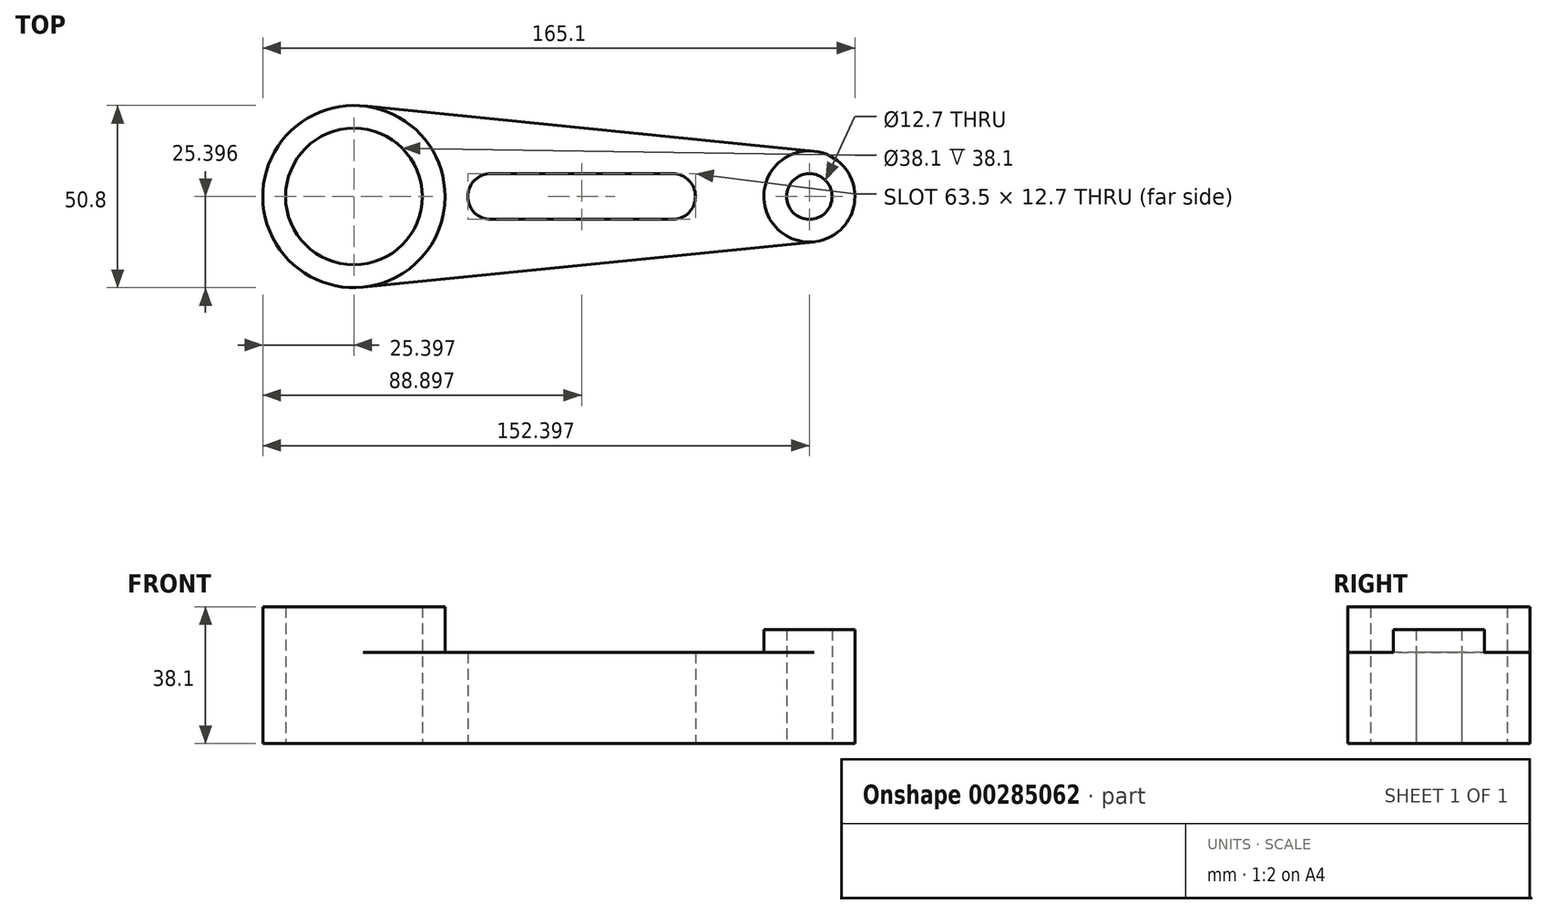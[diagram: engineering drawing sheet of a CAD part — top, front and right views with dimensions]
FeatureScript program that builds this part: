
annotation { "Feature Type Name" : "Feature", "Feature Type Description" : "" }
export const myFeature = defineFeature(function(context is Context, id is Id, definition is map)
    precondition{}
    {
        {
            var Q0;
            Q0=qCreatedBy(makeId("Top.planeOp"),FACE);
            var sketch = newSketch(context, id + "F0", { "sketchPlane" : qUnion([Q0])});
            skCircle(sketch, "E0", {"center": v(-46.28, 18.05) * mm, "radius": 25.4 * mm});
            skCircle(sketch, "E1", {"center": v(-46.28, 18.05) * mm, "radius": 19.05 * mm});
            skArc(sketch, "E2", {"start": v(-8.18, 24.4) * mm, "mid": v(-14.53, 18.05) * mm, "end": v(-8.18, 11.7) * mm});
            skArc(sketch, "E3", {"start": v(42.62, 11.7) * mm, "mid": v(48.97, 18.05) * mm, "end": v(42.62, 24.4) * mm});
            skCircle(sketch, "E4", {"center": v(80.72, 18.05) * mm, "radius": 6.35 * mm});
            skCircle(sketch, "E5", {"center": v(80.72, 18.05) * mm, "radius": 12.7 * mm});
            skLineSegment(sketch, "E6", {"start": v(-8.18, 24.4) * mm, "end": v(42.62, 24.4) * mm});
            skLineSegment(sketch, "E7", {"start": v(-8.18, 11.7) * mm, "end": v(42.62, 11.7) * mm});
            skLineSegment(sketch, "E8", {"start": v(-43.74, 43.32) * mm, "end": v(81.99, 30.68) * mm});
            skLineSegment(sketch, "E9", {"start": v(-43.74, -7.23) * mm, "end": v(81.99, 5.4) * mm});
            skSolve(sketch);
        }
        {
            var Q0;
            Q0=makeQuery(id+"F0.imprint","IMPRINT",FACE,{"disambiguationData":[TD([[makeQuery(id+"F0.imprint","IMPRINT",EDGE,{"derivedFrom":sQuery(id+"F0.wireOp",EDGE,"E2")}),-1.0]])]});
            var Q1;
            Q1=makeQuery(id+"F0.imprint","IMPRINT",FACE,{"disambiguationData":[TD([[makeQuery(id+"F0.imprint","IMPRINT",EDGE,{"derivedFrom":sQuery(id+"F0.wireOp",EDGE,"E1")}),-1.0]])]});
            var Q2;
            Q2=makeQuery(id+"F0.imprint","IMPRINT",FACE,{"disambiguationData":[TD([[makeQuery(id+"F0.imprint","IMPRINT",EDGE,{"derivedFrom":sQuery(id+"F0.wireOp",EDGE,"E4")}),-1.0]])]});
            extrude(context, id + "F1", {"entities" : qUnion([Q0, Q1, Q2]), "depth" : 25.4 * mm});
        }
        {
            var Q0;
            Q0=makeQuery(id+"F0.imprint","IMPRINT",FACE,{"disambiguationData":[TD([[makeQuery(id+"F0.imprint","IMPRINT",EDGE,{"derivedFrom":sQuery(id+"F0.wireOp",EDGE,"E1")}),-1.0]])]});
            extrude(context, id + "F2", {"entities" : qUnion([Q0]), "operationType" : NewBodyOperationType.ADD, "depth" : 38.1 * mm});
        }
        {
            var Q0;
            Q0=makeQuery(id+"F0.imprint","IMPRINT",FACE,{"disambiguationData":[TD([[makeQuery(id+"F0.imprint","IMPRINT",EDGE,{"derivedFrom":sQuery(id+"F0.wireOp",EDGE,"E4")}),-1.0]])]});
            extrude(context, id + "F3", {"entities" : qUnion([Q0]), "operationType" : NewBodyOperationType.ADD, "depth" : 31.75 * mm});
        }
    });
